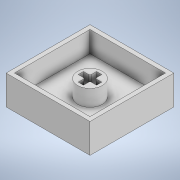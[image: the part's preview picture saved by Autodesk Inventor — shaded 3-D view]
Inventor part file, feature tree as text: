
AUTODESK INVENTOR PART (.ipt)
format: ipt  version: 2021.1 (Build 251245000, 245)  size: 136,192 bytes
history: native  units: mm
features: extrude x3, sketch x3, fillet x1
ambient origin geometry x8: Origin, YZ Plane, XZ Plane, XY Plane, X Axis, Y Axis, Z Axis, Center Point
bodies: Solid1 (feature_tree)
feature tree (7):
  extrude  "Extrusion1"  Depth=5.0mm TaperAngle=0.0deg
  extrude  "Extrusion2"  Depth=0.3mm
  extrude  "Extrusion4"  [1 undecoded]
  fillet  "Fillet1"  [1 undecoded]
  sketch  "Sketch1"  dims[d0=2.0mm d1=0.0mm d2=5.0mm d3=0.0mm]
  sketch  "Sketch2"  dims[d11=3.9mm d12=0.0mm d13=0.3mm]
  sketch  "Sketch3"
note: 2 required parameter values undecoded (feature->parameter linkage not recoverable at this tier; creation-order binding heuristic only, values carry confidence <= 0.55)
